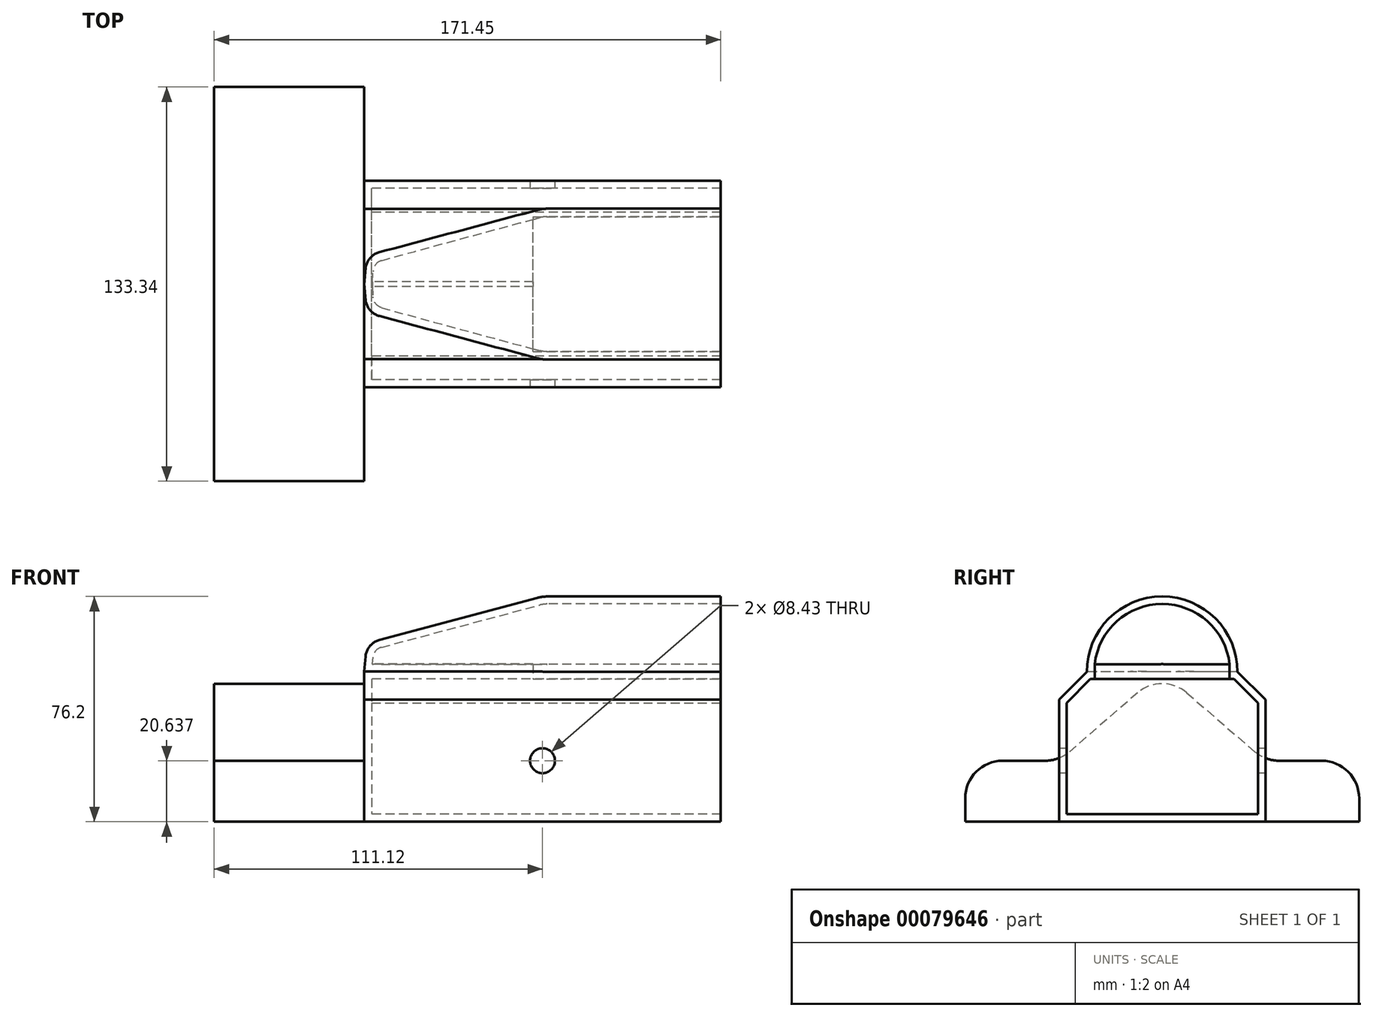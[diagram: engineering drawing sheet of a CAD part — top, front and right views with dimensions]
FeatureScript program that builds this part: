
annotation { "Feature Type Name" : "Feature", "Feature Type Description" : "" }
export const myFeature = defineFeature(function(context is Context, id is Id, definition is map)
    precondition{}
    {
        {
            var Q0;
            Q0=qCreatedBy(makeId("Top.planeOp"),FACE);
            var sketch = newSketch(context, id + "F0", { "sketchPlane" : qUnion([Q0])});
            skLineSegment(sketch, "E0.bottom", {"start": v(60.33, -34.92) * mm, "end": v(-60.32, -34.92) * mm});
            skLineSegment(sketch, "E0.top", {"start": v(60.32, 34.93) * mm, "end": v(-60.33, 34.93) * mm});
            skLineSegment(sketch, "E0.left", {"start": v(60.33, -34.92) * mm, "end": v(60.32, 34.93) * mm});
            skLineSegment(sketch, "E0.right", {"start": v(-60.32, -34.92) * mm, "end": v(-60.33, 34.93) * mm});
            skPoint(sketch, "E0.middle", {"position": v(0, 0) * mm});
            skSolve(sketch);
        }
        {
            var Q0;
            Q0=makeQuery(id+"F0.imprint","IMPRINT",FACE,{"disambiguationData":[TD([[makeQuery(id+"F0.imprint","IMPRINT",EDGE,{"derivedFrom":sQuery(id+"F0.wireOp",EDGE,"E0.bottom")}),-1.0]])]});
            extrude(context, id + "F1", {"entities" : qUnion([Q0]), "depth" : 50.8 * mm});
        }
        {
            var Q0;
            Q0=makeQuery(id+"F1.opExtrude","CAP_EDGE",EDGE,{"disambiguationData":[OSD([sQuery(id+"F0.wireOp",EDGE,"E0.bottom")])],"isStart":false});
            var Q1;
            Q1=makeQuery(id+"F1.opExtrude","CAP_EDGE",EDGE,{"disambiguationData":[OSD([sQuery(id+"F0.wireOp",EDGE,"E0.top")])],"isStart":false});
            chamfer(context, id + "F2", {"entities" : qUnion([Q0, Q1]), "width" : 9.52 * mm, "tangentPropagation" : true});
        }
        {
            var Q0;
            Q0=makeQuery(id+"F1.opExtrude","SWEPT_FACE",FACE,{"disambiguationData":[OSD([sQuery(id+"F0.wireOp",EDGE,"E0.left")])]});
            shell(context, id + "F3", {"entities" : qUnion([Q0]), "thickness" : 2.54 * mm});
        }
        {
            var Q0;
            Q0=makeQuery(id+"F1.opExtrude","SWEPT_FACE",FACE,{"disambiguationData":[OSD([sQuery(id+"F0.wireOp",EDGE,"E0.bottom")])]});
            var sketch = newSketch(context, id + "F4", { "sketchPlane" : qUnion([Q0])});
            skPoint(sketch, "E1", {"position": v(0, 20.64) * mm});
            skPoint(sketch, "E1.positionSnap0", {"position": v(60.33, 20.64) * mm});
            skPoint(sketch, "E1.positionSnap1", {"position": v(0, 41.28) * mm});
            skSolve(sketch);
        }
        {
            var Q0;
            Q0=sQuery(id+"F4.wireOp",VERTEX,"E1");
            var Q1;
            Q1=makeQuery(id+"F1.opExtrude","SWEPT_BODY",BODY,{"disambiguationData":[OSD([sQuery(id+"F0.wireOp",EDGE,"E0.bottom"),sQuery(id+"F0.wireOp",EDGE,"E0.top"),sQuery(id+"F0.wireOp",EDGE,"E0.left"),sQuery(id+"F0.wireOp",EDGE,"E0.right")])]});
            hole(context, id + "F5", {"style" : HoleStyle.SIMPLE, "endStyle" : HoleEndStyle.THROUGH, "standardTappedOrClearance" : lookupTablePath({ "standard" : "ANSI", "fit" : "Normal (ASME)", "size" : "5/16", "type" : "Clearance" }), "standardBlindInLast" : lookupTablePath({ "fit" : "Free", "standard" : "ANSI", "size" : "5/16", "type" : "Clearance" }), "holeDiameter" : 8.43 * mm, "locations" : qUnion([Q0]), "scope" : qUnion([Q1]), "isTappedThrough" : true});
        }
        {
            var Q0;
            Q0=qCreatedBy(makeId("Front.planeOp"),FACE);
            var sketch = newSketch(context, id + "F6", { "sketchPlane" : qUnion([Q0])});
            skLineSegment(sketch, "E2", {"start": v(-60.33, 50.8) * mm, "end": v(-59.87, 55.9) * mm});
            skLineSegment(sketch, "E3", {"start": v(-55.19, 61.47) * mm, "end": v(-1.6, 75.77) * mm});
            skLineSegment(sketch, "E4", {"start": v(1.67, 76.2) * mm, "end": v(60.32, 76.2) * mm});
            skLineSegment(sketch, "E5", {"start": v(60.32, 76.2) * mm, "end": v(60.32, 50.8) * mm});
            skArc(sketch, "E6", {"start": v(-55.19, 61.47) * mm, "mid": v(-58.4, 59.42) * mm, "end": v(-59.87, 55.9) * mm});
            skPoint(sketch, "E7.orphan", {"position": v(-59.48, 60.33) * mm});
            skArc(sketch, "E8", {"start": v(1.67, 76.2) * mm, "mid": v(0.01, 76.1) * mm, "end": v(-1.6, 75.77) * mm});
            skPoint(sketch, "E9.orphan", {"position": v(0, 76.2) * mm});
            skLineSegment(sketch, "E10", {"start": v(-60.33, 50.8) * mm, "end": v(60.32, 50.8) * mm});
            skSolve(sketch);
        }
        {
            var Q0;
            Q0=qCreatedBy(makeId("Front.planeOp"),FACE);
            var sketch = newSketch(context, id + "F7", { "sketchPlane" : qUnion([Q0])});
            skLineSegment(sketch, "E11", {"start": v(-107.32, 50.68) * mm, "end": v(96.85, 50.68) * mm, "construction": true});
            skSolve(sketch);
        }
        {
            var Q0;
            Q0 = qSketchRegion(id + "F6", true);
            var Q1;
            Q1=sQuery(id+"F7.wireOp",EDGE,"E11");
            revolve(context, id + "F8", {"entities" : qUnion([Q0]), "axis" : qUnion([Q1]), "revolveType" : RevolveType.SYMMETRIC, "angle" : 180 * degree});
        }
        {
            var Q0;
            Q0=makeQuery(id+"F8.opRevolve","SWEPT_FACE",FACE,{"disambiguationData":[OSD([sQuery(id+"F6.wireOp",EDGE,"E5")])]});
            shell(context, id + "F9", {"entities" : qUnion([Q0]), "thickness" : 2.54 * mm});
        }
        {
            var Q0;
            Q0=makeQuery(id+"F8.opRevolve","SWEPT_BODY",BODY,{"disambiguationData":[OSD([sQuery(id+"F6.wireOp",EDGE,"E2"),sQuery(id+"F6.wireOp",EDGE,"E3"),sQuery(id+"F6.wireOp",EDGE,"E4"),sQuery(id+"F6.wireOp",EDGE,"E5"),sQuery(id+"F6.wireOp",EDGE,"E6"),sQuery(id+"F6.wireOp",EDGE,"E8"),sQuery(id+"F6.wireOp",EDGE,"E10")])]});
            var Q1;
            Q1=makeQuery(id+"F1.opExtrude","SWEPT_BODY",BODY,{"disambiguationData":[OSD([sQuery(id+"F0.wireOp",EDGE,"E0.bottom"),sQuery(id+"F0.wireOp",EDGE,"E0.top"),sQuery(id+"F0.wireOp",EDGE,"E0.left"),sQuery(id+"F0.wireOp",EDGE,"E0.right")])]});
            booleanBodies(context, id + "F10", {"operationType" : BooleanOperationType.UNION, "tools" : qUnion([Q0, Q1])});
        }
        {
            var Q0;
            Q0=makeQuery(id+"F10.opBoolean","MERGE",FACE,{"derivedFrom":[makeQuery(id+"F1.opExtrude","SWEPT_FACE",FACE,{"disambiguationData":[OSD([sQuery(id+"F0.wireOp",EDGE,"E0.left")])]}),makeQuery(id+"F8.opRevolve","SWEPT_FACE",FACE,{"disambiguationData":[OSD([sQuery(id+"F6.wireOp",EDGE,"E5")])]})]});
            var sketch = newSketch(context, id + "F11", { "sketchPlane" : qUnion([Q0])});
            skLineSegment(sketch, "E12.bottom", {"start": v(22.84, 53.22) * mm, "end": v(5.55, 53.22) * mm});
            skLineSegment(sketch, "E12.top", {"start": v(22.84, 48.14) * mm, "end": v(-22.84, 48.14) * mm});
            skLineSegment(sketch, "E12.left", {"start": v(22.84, 53.22) * mm, "end": v(22.84, 48.14) * mm});
            skLineSegment(sketch, "E12.right", {"start": v(-22.84, 53.22) * mm, "end": v(-22.84, 48.14) * mm});
            skPoint(sketch, "E12.middle", {"position": v(0, 50.68) * mm});
            skLineSegment(sketch, "E13.bottom", {"start": v(5.55, 55.53) * mm, "end": v(-5.55, 55.53) * mm});
            skLineSegment(sketch, "E13.left", {"start": v(5.55, 55.53) * mm, "end": v(5.55, 53.22) * mm});
            skLineSegment(sketch, "E13.right", {"start": v(-5.55, 55.53) * mm, "end": v(-5.55, 53.22) * mm});
            skPoint(sketch, "E13.middle", {"position": v(0, 53.22) * mm});
            skLineSegment(sketch, "E14.trimOffspring", {"start": v(-5.55, 53.22) * mm, "end": v(-22.84, 53.22) * mm});
            skPoint(sketch, "E15.orphan", {"position": v(5.55, 50.9) * mm});
            skPoint(sketch, "E16.orphan", {"position": v(-5.55, 50.9) * mm});
            skSolve(sketch);
        }
        {
            var Q0;
            Q0 = qSketchRegion(id + "F11", true);
            extrude(context, id + "F12", {"entities" : qUnion([Q0]), "operationType" : NewBodyOperationType.REMOVE, "oppositeDirection" : true, "depth" : 63.5 * mm});
        }
        {
            var Q0;
            Q0=makeQuery(id+"F1.opExtrude","SWEPT_FACE",FACE,{"disambiguationData":[OSD([sQuery(id+"F0.wireOp",EDGE,"E0.right")])]});
            var sketch = newSketch(context, id + "F14", { "sketchPlane" : qUnion([Q0])});
            skLineSegment(sketch, "E17", {"start": v(0, 50.8) * mm, "end": v(34.92, 20.64) * mm});
            skLineSegment(sketch, "E18", {"start": v(34.92, 20.64) * mm, "end": v(34.92, 20.64) * mm});
            skLineSegment(sketch, "E19", {"start": v(66.67, 20.64) * mm, "end": v(34.92, 20.64) * mm});
            skLineSegment(sketch, "E20", {"start": v(66.67, 0) * mm, "end": v(66.67, 20.64) * mm});
            skLineSegment(sketch, "E21", {"start": v(66.67, 0) * mm, "end": v(0, 0) * mm});
            skLineSegment(sketch, "E22", {"start": v(0, 102.12) * mm, "end": v(0, 0) * mm, "construction": true});
            skLineSegment(sketch, "E23.MirrorCS", {"start": v(0, 50.8) * mm, "end": v(-34.92, 20.64) * mm});
            skLineSegment(sketch, "E24.MirrorCS", {"start": v(-66.67, 20.64) * mm, "end": v(-34.92, 20.64) * mm});
            skLineSegment(sketch, "E25.MirrorCS", {"start": v(-66.67, 0) * mm, "end": v(0, 0) * mm});
            skLineSegment(sketch, "E26.MirrorCS", {"start": v(-66.67, 0) * mm, "end": v(-66.67, 20.64) * mm});
            skSolve(sketch);
        }
        {
            var Q0;
            Q0 = qSketchRegion(id + "F14", true);
            extrude(context, id + "F15", {"entities" : qUnion([Q0]), "operationType" : NewBodyOperationType.ADD, "depth" : 50.8 * mm});
        }
        {
            var Q0;
            Q0=makeQuery(id+"F15.opExtrude","SWEPT_EDGE",EDGE,{"disambiguationData":[OSD([sQuery(id+"F14.wireOp",EDGE,"E19"),sQuery(id+"F14.wireOp",EDGE,"E20")])]});
            var Q1;
            Q1=makeQuery(id+"F15.opExtrude","SWEPT_EDGE",EDGE,{"disambiguationData":[OSD([sQuery(id+"F0.wireOp",EDGE,"E0.bottom"),sQuery(id+"F0.wireOp",EDGE,"E0.right"),sQuery(id+"F14.wireOp",EDGE,"E17"),sQuery(id+"F14.wireOp",EDGE,"E19")])]});
            var Q2;
            Q2=makeQuery(id+"F15.opExtrude","SWEPT_EDGE",EDGE,{"disambiguationData":[OSD([sQuery(id+"F0.wireOp",EDGE,"E0.right"),sQuery(id+"F14.wireOp",EDGE,"E17"),sQuery(id+"F14.wireOp",EDGE,"E23.MirrorCS")])]});
            var Q3;
            Q3=makeQuery(id+"F15.opExtrude","SWEPT_EDGE",EDGE,{"disambiguationData":[OSD([sQuery(id+"F0.wireOp",EDGE,"E0.top"),sQuery(id+"F0.wireOp",EDGE,"E0.right"),sQuery(id+"F14.wireOp",EDGE,"E23.MirrorCS"),sQuery(id+"F14.wireOp",EDGE,"E24.MirrorCS")])]});
            var Q4;
            Q4=makeQuery(id+"F15.opExtrude","SWEPT_EDGE",EDGE,{"disambiguationData":[OSD([sQuery(id+"F14.wireOp",EDGE,"E24.MirrorCS"),sQuery(id+"F14.wireOp",EDGE,"E26.MirrorCS")])]});
            fillet(context, id + "F13", {"entities" : qUnion([Q0, Q1, Q2, Q3, Q4]), "radius" : 12.7 * mm, "tangentPropagation" : true, "allowEdgeOverflow" : false});
        }
    });
